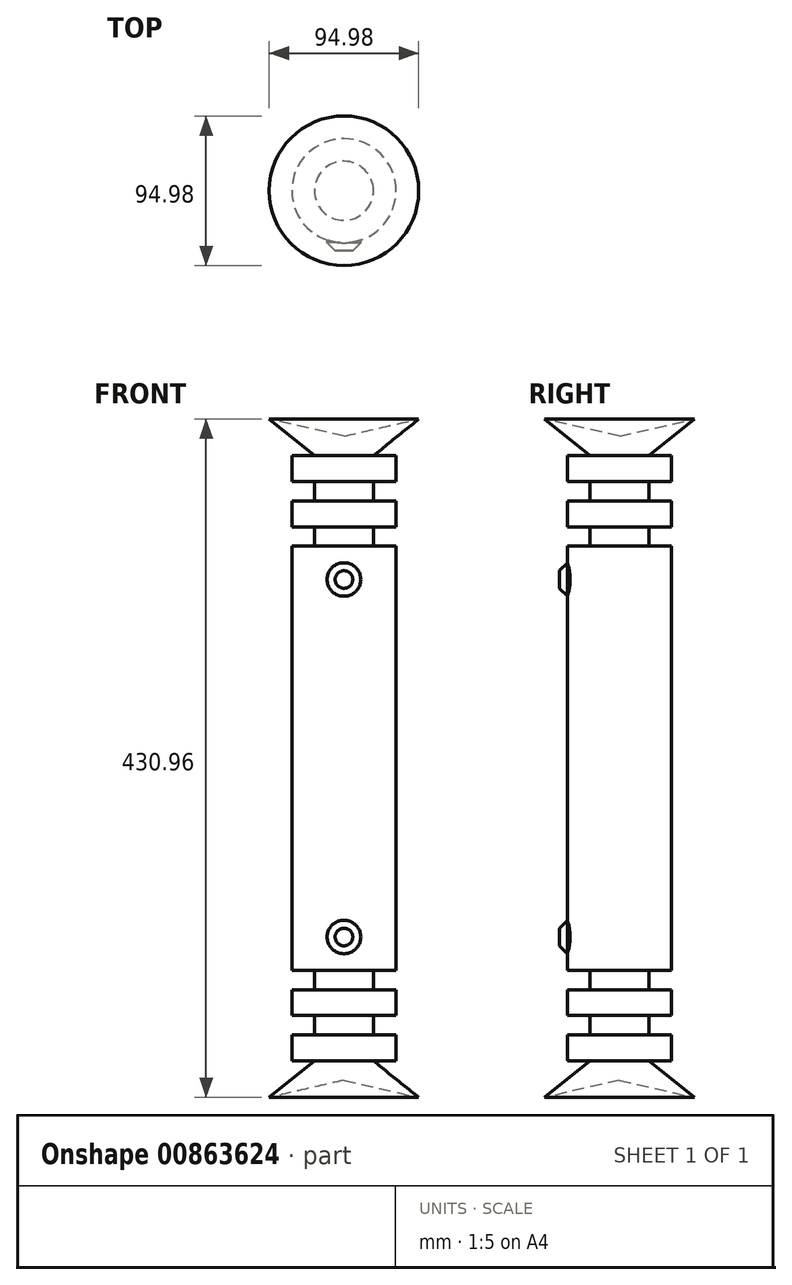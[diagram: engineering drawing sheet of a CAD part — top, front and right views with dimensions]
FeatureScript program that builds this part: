
annotation { "Feature Type Name" : "Feature", "Feature Type Description" : "" }
export const myFeature = defineFeature(function(context is Context, id is Id, definition is map)
    precondition{}
    {
        {
            var Q0;
            Q0=qCreatedBy(makeId("Front.planeOp"),FACE);
            var sketch = newSketch(context, id + "F0", { "sketchPlane" : qUnion([Q0])});
            skLineSegment(sketch, "E0", {"start": v(0, 0) * mm, "end": v(0, -204.53) * mm});
            skLineSegment(sketch, "E1", {"start": v(0, -204.53) * mm, "end": v(47.49, -215.48) * mm});
            skLineSegment(sketch, "E2", {"start": v(47.49, -215.48) * mm, "end": v(18.74, -192.2) * mm});
            skLineSegment(sketch, "E3", {"start": v(18.74, -192.2) * mm, "end": v(33.11, -192.2) * mm});
            skPoint(sketch, "E3.endSnap0", {"position": v(33.11, -203.84) * mm});
            skLineSegment(sketch, "E4", {"start": v(33.11, -192.2) * mm, "end": v(33.11, -175.78) * mm});
            skLineSegment(sketch, "E5", {"start": v(18.74, -175.78) * mm, "end": v(33.11, -175.78) * mm});
            skLineSegment(sketch, "E6", {"start": v(18.74, -175.78) * mm, "end": v(18.74, -163.45) * mm});
            skLineSegment(sketch, "E7", {"start": v(33.11, -163.45) * mm, "end": v(18.74, -163.45) * mm});
            skLineSegment(sketch, "E8", {"start": v(33.11, -163.45) * mm, "end": v(33.11, -147.03) * mm});
            skLineSegment(sketch, "E9", {"start": v(33.11, -147.03) * mm, "end": v(18.74, -147.03) * mm});
            skLineSegment(sketch, "E10", {"start": v(18.74, -147.03) * mm, "end": v(18.74, -134.7) * mm});
            skLineSegment(sketch, "E11", {"start": v(18.74, -134.7) * mm, "end": v(33.11, -134.7) * mm});
            skLineSegment(sketch, "E12", {"start": v(33.11, -134.7) * mm, "end": v(33.11, 0) * mm});
            skLineSegment(sketch, "E13", {"start": v(0, 0) * mm, "end": v(33.11, 0) * mm});
            skLineSegment(sketch, "E14.MirrorCS", {"start": v(33.11, 163.45) * mm, "end": v(18.74, 163.45) * mm});
            skLineSegment(sketch, "E15.MirrorCS", {"start": v(18.74, 175.78) * mm, "end": v(33.11, 175.78) * mm});
            skLineSegment(sketch, "E16.MirrorCS", {"start": v(33.11, 163.45) * mm, "end": v(33.11, 147.03) * mm});
            skLineSegment(sketch, "E17.MirrorCS", {"start": v(18.74, 175.78) * mm, "end": v(18.74, 163.45) * mm});
            skLineSegment(sketch, "E18.MirrorCS", {"start": v(18.74, 192.2) * mm, "end": v(33.11, 192.2) * mm});
            skLineSegment(sketch, "E19.MirrorCS", {"start": v(33.11, 192.2) * mm, "end": v(33.11, 175.78) * mm});
            skLineSegment(sketch, "E20.MirrorCS", {"start": v(18.74, 134.7) * mm, "end": v(33.11, 134.7) * mm});
            skLineSegment(sketch, "E21.MirrorCS", {"start": v(18.74, 147.03) * mm, "end": v(18.74, 134.7) * mm});
            skLineSegment(sketch, "E22.MirrorCS", {"start": v(33.11, 147.03) * mm, "end": v(18.74, 147.03) * mm});
            skLineSegment(sketch, "E23.MirrorCS", {"start": v(47.49, 215.48) * mm, "end": v(18.74, 192.2) * mm});
            skLineSegment(sketch, "E24.MirrorCS", {"start": v(0, 204.53) * mm, "end": v(47.49, 215.48) * mm});
            skPoint(sketch, "E25.MirrorP", {"position": v(33.11, 203.84) * mm});
            skLineSegment(sketch, "E26.MirrorCS", {"start": v(33.11, 134.7) * mm, "end": v(33.11, 0) * mm});
            skLineSegment(sketch, "E27.MirrorCS", {"start": v(0, 0) * mm, "end": v(0, 204.53) * mm});
            skSolve(sketch);
        }
        {
            var Q0;
            Q0=makeQuery(id+"F0.imprint","IMPRINT",FACE,{"disambiguationData":[TD([[makeQuery(id+"F0.imprint","IMPRINT",EDGE,{"derivedFrom":sQuery(id+"F0.wireOp",EDGE,"E0")}),1.0]])]});
            var Q1;
            Q1=makeQuery(id+"F0.imprint","IMPRINT",FACE,{"disambiguationData":[TD([[makeQuery(id+"F0.imprint","IMPRINT",EDGE,{"derivedFrom":sQuery(id+"F0.wireOp",EDGE,"E13")}),1.0]])]});
            var Q2;
            Q2=sQuery(id+"F0.wireOp",EDGE,"E0");
            revolve(context, id + "F1", {"surfaceOperationType" : NewSurfaceOperationType.NEW, "entities" : qUnion([Q0, Q1]), "axis" : qUnion([Q2]), "revolveType" : RevolveType.FULL});
        }
        {
            var Q0;
            Q0=qCreatedBy(makeId("Front.planeOp"),FACE);
            var sketch = newSketch(context, id + "F2", { "sketchPlane" : qUnion([Q0])});
            skCircle(sketch, "E28", {"center": v(0, 113.53) * mm, "radius": 10.68 * mm});
            skCircle(sketch, "E29.MirrorC", {"center": v(0, -113.53) * mm, "radius": 10.68 * mm});
            skSolve(sketch);
        }
        {
            var Q0;
            Q0 = qSketchRegion(id + "F2", true);
            extrude(context, id + "F3", {"entities" : qUnion([Q0]), "operationType" : NewBodyOperationType.ADD, "depth" : 38.1 * mm, "offsetDistance" : 25.4 * mm});
        }
        {
            var Q0;
            Q0=makeQuery(id+"F3.opExtrude","CAP_EDGE",EDGE,{"disambiguationData":[OSD([sQuery(id+"F2.wireOp",EDGE,"E28")])],"isStart":false});
            var Q1;
            Q1=makeQuery(id+"F3.opExtrude","CAP_EDGE",EDGE,{"disambiguationData":[OSD([sQuery(id+"F2.wireOp",EDGE,"E29.MirrorC")])],"isStart":false});
            chamfer(context, id + "F4", {"entities" : qUnion([Q0, Q1]), "chamferType" : ChamferType.OFFSET_ANGLE, "width" : 5.08 * mm, "oppositeDirection" : false, "angle" : 45 * degree, "tangentPropagation" : true});
        }
    });
